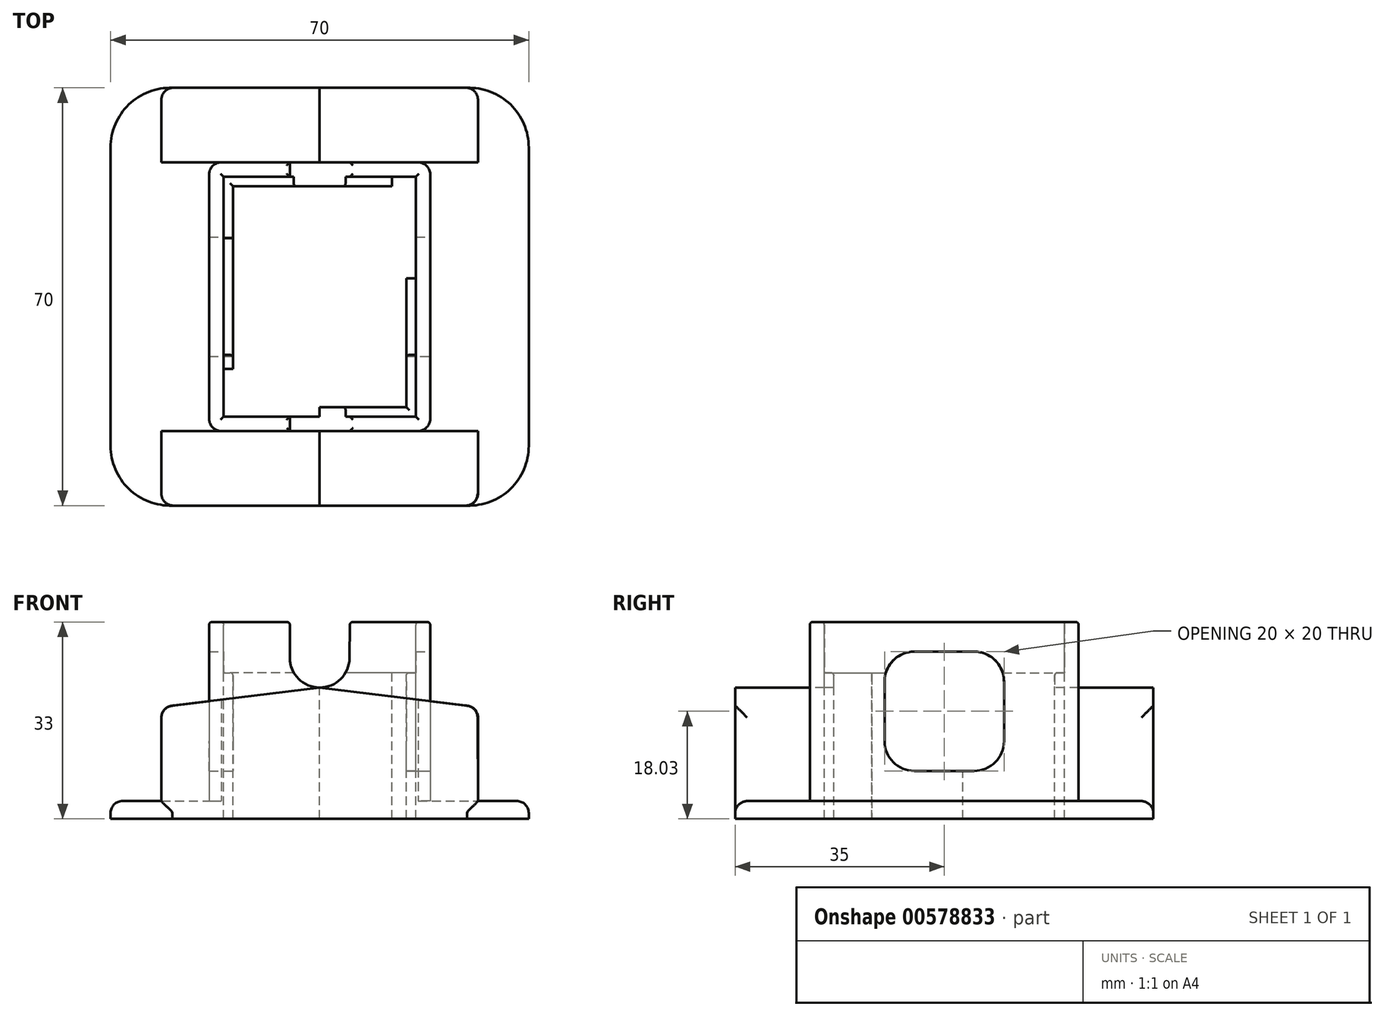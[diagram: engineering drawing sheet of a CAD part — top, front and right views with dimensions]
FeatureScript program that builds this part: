
annotation { "Feature Type Name" : "Feature", "Feature Type Description" : "" }
export const myFeature = defineFeature(function(context is Context, id is Id, definition is map)
    precondition{}
    {
        {
            var Q0;
            Q0=qCreatedBy(makeId("Top.planeOp"),FACE);
            var sketch = newSketch(context, id + "F0", { "sketchPlane" : qUnion([Q0])});
            skLineSegment(sketch, "E0.bottom", {"start": v(25, -35) * mm, "end": v(-25, -35) * mm});
            skLineSegment(sketch, "E0.top", {"start": v(25, 35) * mm, "end": v(-25, 35) * mm});
            skLineSegment(sketch, "E0.left", {"start": v(35, -25) * mm, "end": v(35, 25) * mm});
            skLineSegment(sketch, "E0.right", {"start": v(-35, -25) * mm, "end": v(-35, 25) * mm});
            skPoint(sketch, "E0.middle", {"position": v(0, 0) * mm});
            skPoint(sketch, "E1.visualSharp", {"position": v(-35, -35) * mm});
            skArc(sketch, "E1.filletArc", {"start": v(-35, -25) * mm, "mid": v(-32.07, -32.07) * mm, "end": v(-25, -35) * mm});
            skPoint(sketch, "E2.visualSharp", {"position": v(35, -35) * mm});
            skArc(sketch, "E2.filletArc", {"start": v(25, -35) * mm, "mid": v(32.07, -32.07) * mm, "end": v(35, -25) * mm});
            skPoint(sketch, "E3.visualSharp", {"position": v(35, 35) * mm});
            skArc(sketch, "E3.filletArc", {"start": v(35, 25) * mm, "mid": v(32.07, 32.07) * mm, "end": v(25, 35) * mm});
            skPoint(sketch, "E4.visualSharp", {"position": v(-35, 35) * mm});
            skArc(sketch, "E4.filletArc", {"start": v(-25, 35) * mm, "mid": v(-32.07, 32.07) * mm, "end": v(-35, 25) * mm});
            skSolve(sketch);
        }
        {
            var Q0;
            Q0=qSketchRegion(id+"F0",true);
            extrude(context, id + "F1", {"entities" : qUnion([Q0]), "depth" : 3 * mm, "offsetDistance" : 25 * mm});
        }
        {
            var Q0;
            Q0=makeQuery(id+"F1.opExtrude","CAP_FACE",FACE,{"disambiguationData":[OSD([sQuery(id+"F0.wireOp",EDGE,"E0.bottom"),sQuery(id+"F0.wireOp",EDGE,"E0.top"),sQuery(id+"F0.wireOp",EDGE,"E0.left"),sQuery(id+"F0.wireOp",EDGE,"E0.right"),sQuery(id+"F0.wireOp",EDGE,"E1.filletArc"),sQuery(id+"F0.wireOp",EDGE,"E2.filletArc"),sQuery(id+"F0.wireOp",EDGE,"E3.filletArc"),sQuery(id+"F0.wireOp",EDGE,"E4.filletArc")])],"isStart":false});
            var sketch = newSketch(context, id + "F2", { "sketchPlane" : qUnion([Q0])});
            skLineSegment(sketch, "E5.bottom", {"start": v(16.5, -22.5) * mm, "end": v(-16.5, -22.5) * mm});
            skLineSegment(sketch, "E5.top", {"start": v(16.5, 22.5) * mm, "end": v(-16.5, 22.5) * mm});
            skLineSegment(sketch, "E5.left", {"start": v(18.5, -20.5) * mm, "end": v(18.5, 20.5) * mm});
            skLineSegment(sketch, "E5.right", {"start": v(-18.5, -20.5) * mm, "end": v(-18.5, 20.5) * mm});
            skPoint(sketch, "E5.middle", {"position": v(0, 0) * mm});
            skPoint(sketch, "E6.visualSharp", {"position": v(18.5, -22.5) * mm});
            skArc(sketch, "E6.filletArc", {"start": v(16.5, -22.5) * mm, "mid": v(17.91, -21.91) * mm, "end": v(18.5, -20.5) * mm});
            skPoint(sketch, "E7.visualSharp", {"position": v(18.5, 22.5) * mm});
            skArc(sketch, "E7.filletArc", {"start": v(18.5, 20.5) * mm, "mid": v(17.91, 21.91) * mm, "end": v(16.5, 22.5) * mm});
            skPoint(sketch, "E8.visualSharp", {"position": v(-18.5, 22.5) * mm});
            skArc(sketch, "E8.filletArc", {"start": v(-16.5, 22.5) * mm, "mid": v(-17.91, 21.91) * mm, "end": v(-18.5, 20.5) * mm});
            skPoint(sketch, "E9.visualSharp", {"position": v(-18.5, -22.5) * mm});
            skArc(sketch, "E9.filletArc", {"start": v(-18.5, -20.5) * mm, "mid": v(-17.91, -21.91) * mm, "end": v(-16.5, -22.5) * mm});
            skSolve(sketch);
        }
        {
            var Q0;
            Q0=makeQuery(id+"F2.imprint","IMPRINT",FACE,{"disambiguationData":[TD([[makeQuery(id+"F2.imprint","IMPRINT",EDGE,{"derivedFrom":sQuery(id+"F2.wireOp",EDGE,"E5.bottom")}),-1.0]])]});
            extrude(context, id + "F3", {"entities" : qUnion([Q0]), "operationType" : NewBodyOperationType.ADD, "depth" : 30 * mm, "offsetDistance" : 25 * mm});
        }
        {
            var Q0;
            Q0=makeQuery(id+"F3.opExtrude","CAP_FACE",FACE,{"disambiguationData":[OSD([sQuery(id+"F2.wireOp",EDGE,"E5.bottom"),sQuery(id+"F2.wireOp",EDGE,"E5.top"),sQuery(id+"F2.wireOp",EDGE,"E5.left"),sQuery(id+"F2.wireOp",EDGE,"E5.right"),sQuery(id+"F2.wireOp",EDGE,"E6.filletArc"),sQuery(id+"F2.wireOp",EDGE,"E7.filletArc"),sQuery(id+"F2.wireOp",EDGE,"E8.filletArc"),sQuery(id+"F2.wireOp",EDGE,"E9.filletArc")])],"isStart":false});
            var sketch = newSketch(context, id + "F4", { "sketchPlane" : qUnion([Q0])});
            skLineSegment(sketch, "E10.bottom", {"start": v(-14.5, 18.5) * mm, "end": v(14.5, 18.5) * mm});
            skLineSegment(sketch, "E10.top", {"start": v(-14.5, -18.5) * mm, "end": v(14.5, -18.5) * mm});
            skLineSegment(sketch, "E10.left", {"start": v(-14.5, 18.5) * mm, "end": v(-14.5, -18.5) * mm});
            skLineSegment(sketch, "E10.right", {"start": v(14.5, 18.5) * mm, "end": v(14.5, -18.5) * mm});
            skPoint(sketch, "E10.middle", {"position": v(0, 0) * mm});
            skSolve(sketch);
        }
        {
            var Q0;
            Q0=makeQuery(id+"F4.imprint","IMPRINT",FACE,{"disambiguationData":[TD([[makeQuery(id+"F4.imprint","IMPRINT",EDGE,{"derivedFrom":sQuery(id+"F4.wireOp",EDGE,"E10.bottom")}),-1.0]])]});
            extrude(context, id + "F5", {"entities" : qUnion([Q0]), "operationType" : NewBodyOperationType.REMOVE, "endBound" : BoundingType.THROUGH_ALL, "oppositeDirection" : true, "depth" : 25 * mm});
        }
        {
            var Q0;
            Q0=makeQuery(id+"F3.opExtrude","CAP_FACE",FACE,{"disambiguationData":[OSD([sQuery(id+"F2.wireOp",EDGE,"E5.bottom"),sQuery(id+"F2.wireOp",EDGE,"E5.top"),sQuery(id+"F2.wireOp",EDGE,"E5.left"),sQuery(id+"F2.wireOp",EDGE,"E5.right"),sQuery(id+"F2.wireOp",EDGE,"E6.filletArc"),sQuery(id+"F2.wireOp",EDGE,"E7.filletArc"),sQuery(id+"F2.wireOp",EDGE,"E8.filletArc"),sQuery(id+"F2.wireOp",EDGE,"E9.filletArc")])],"isStart":false});
            var sketch = newSketch(context, id + "F6", { "sketchPlane" : qUnion([Q0])});
            skLineSegment(sketch, "E11.bottom", {"start": v(16.1, -20.1) * mm, "end": v(-16.1, -20.1) * mm});
            skLineSegment(sketch, "E11.top", {"start": v(16.1, 20.1) * mm, "end": v(-16.1, 20.1) * mm});
            skLineSegment(sketch, "E11.left", {"start": v(16.1, -20.1) * mm, "end": v(16.1, 20.1) * mm});
            skLineSegment(sketch, "E11.right", {"start": v(-16.1, -20.1) * mm, "end": v(-16.1, 20.1) * mm});
            skPoint(sketch, "E11.middle", {"position": v(0, 0) * mm});
            skSolve(sketch);
        }
        {
            var Q0;
            Q0=qSketchRegion(id+"F6",true);
            extrude(context, id + "F7", {"entities" : qUnion([Q0]), "operationType" : NewBodyOperationType.REMOVE, "oppositeDirection" : true, "depth" : 8.5 * mm, "offsetDistance" : 25 * mm});
        }
        {
            var Q0;
            Q0=makeQuery(id+"F7.boolean.opBoolean","COPY",FACE,{"derivedFrom":makeQuery(id+"F7.opExtrude","CAP_FACE",FACE,{"disambiguationData":[OSD([sQuery(id+"F6.wireOp",EDGE,"E11.bottom"),sQuery(id+"F6.wireOp",EDGE,"E11.top"),sQuery(id+"F6.wireOp",EDGE,"E11.left"),sQuery(id+"F6.wireOp",EDGE,"E11.right")])],"isStart":false})});
            var sketch = newSketch(context, id + "F8", { "sketchPlane" : qUnion([Q0])});
            skLineSegment(sketch, "E12.bottom", {"start": v(12.1, 20.1) * mm, "end": v(16.1, 20.1) * mm});
            skLineSegment(sketch, "E12.top", {"start": v(12.1, 3.1) * mm, "end": v(16.1, 3.1) * mm});
            skLineSegment(sketch, "E12.left", {"start": v(12.1, 20.1) * mm, "end": v(12.1, 3.1) * mm});
            skLineSegment(sketch, "E12.right", {"start": v(16.1, 20.1) * mm, "end": v(16.1, 3.1) * mm});
            skSolve(sketch);
        }
        {
            var Q0;
            {var subQ0=sQuery(id+"F8.wireOp",EDGE,"E12.right");var subQ1=sQuery(id+"F8.wireOp",EDGE,"E12.top");var subQ2=makeQuery(id+"F8.imprint","INTERSECT",VERTEX,{"derivedFrom":[subQ1,subQ0]});Q0=makeQuery(id+"F8.imprint","IMPRINT",FACE,{"disambiguationData":[TD([[makeQuery(id+"F8.imprint","IMPRINT",EDGE,{"disambiguationData":[TD([[subQ2,1.0]])],"derivedFrom":subQ1}),1.0]])]});}
            var Q1;
            {var subQ1=sQuery(id+"F8.wireOp",EDGE,"E12.bottom");Q1=makeQuery(id+"F8.imprint","IMPRINT",FACE,{"disambiguationData":[TD([[makeQuery(id+"F8.imprint","IMPRINT",EDGE,{"derivedFrom":subQ1}),1.0]])]});}
            extrude(context, id + "F9", {"entities" : qUnion([Q0, Q1]), "operationType" : NewBodyOperationType.REMOVE, "endBound" : BoundingType.THROUGH_ALL, "oppositeDirection" : true, "depth" : 22 * mm, "offsetDistance" : 25 * mm});
        }
        {
            var Q0;
            Q0=makeQuery(id+"F3.opExtrude","CAP_FACE",FACE,{"disambiguationData":[OSD([sQuery(id+"F2.wireOp",EDGE,"E5.bottom"),sQuery(id+"F2.wireOp",EDGE,"E5.top"),sQuery(id+"F2.wireOp",EDGE,"E5.left"),sQuery(id+"F2.wireOp",EDGE,"E5.right"),sQuery(id+"F2.wireOp",EDGE,"E6.filletArc"),sQuery(id+"F2.wireOp",EDGE,"E7.filletArc"),sQuery(id+"F2.wireOp",EDGE,"E8.filletArc"),sQuery(id+"F2.wireOp",EDGE,"E9.filletArc")])],"isStart":false});
            var sketch = newSketch(context, id + "F10", { "sketchPlane" : qUnion([Q0])});
            skLineSegment(sketch, "E13.bottom", {"start": v(0, -20.1) * mm, "end": v(-16.1, -20.1) * mm});
            skLineSegment(sketch, "E13.top", {"start": v(0, -12.1) * mm, "end": v(-16.1, -12.1) * mm});
            skLineSegment(sketch, "E13.left", {"start": v(0, -20.1) * mm, "end": v(0, -12.1) * mm});
            skLineSegment(sketch, "E13.right", {"start": v(-16.1, -20.1) * mm, "end": v(-16.1, -12.1) * mm});
            skSolve(sketch);
        }
        {
            var Q0;
            Q0=qSketchRegion(id+"F10",true);
            extrude(context, id + "F11", {"entities" : qUnion([Q0]), "operationType" : NewBodyOperationType.REMOVE, "endBound" : BoundingType.THROUGH_ALL, "oppositeDirection" : true, "depth" : 20 * mm, "offsetDistance" : 25 * mm});
        }
        {
            var Q0;
            Q0=makeQuery(id+"F3.opExtrude","SWEPT_FACE",FACE,{"disambiguationData":[OSD([sQuery(id+"F2.wireOp",EDGE,"E5.left")])]});
            var sketch = newSketch(context, id + "F12", { "sketchPlane" : qUnion([Q0])});
            skLineSegment(sketch, "E14.bottom", {"start": v(5, 8.03) * mm, "end": v(-5, 8.03) * mm});
            skLineSegment(sketch, "E14.top", {"start": v(5, 28.03) * mm, "end": v(-5, 28.03) * mm});
            skLineSegment(sketch, "E14.left", {"start": v(10, 13.03) * mm, "end": v(10, 23.03) * mm});
            skLineSegment(sketch, "E14.right", {"start": v(-10, 13.03) * mm, "end": v(-10, 23.03) * mm});
            skPoint(sketch, "E14.middle", {"position": v(0, 18.03) * mm});
            skPoint(sketch, "E15.visualSharp", {"position": v(10, 8.03) * mm});
            skArc(sketch, "E15.filletArc", {"start": v(5, 8.03) * mm, "mid": v(8.54, 9.5) * mm, "end": v(10, 13.03) * mm});
            skPoint(sketch, "E16.visualSharp", {"position": v(-10, 8.03) * mm});
            skArc(sketch, "E16.filletArc", {"start": v(-10, 13.03) * mm, "mid": v(-8.54, 9.5) * mm, "end": v(-5, 8.03) * mm});
            skPoint(sketch, "E17.visualSharp", {"position": v(-10, 28.03) * mm});
            skArc(sketch, "E17.filletArc", {"start": v(-5, 28.03) * mm, "mid": v(-8.54, 26.57) * mm, "end": v(-10, 23.03) * mm});
            skPoint(sketch, "E18.visualSharp", {"position": v(10, 28.03) * mm});
            skArc(sketch, "E18.filletArc", {"start": v(10, 23.03) * mm, "mid": v(8.54, 26.57) * mm, "end": v(5, 28.03) * mm});
            skSolve(sketch);
        }
        {
            var Q0;
            Q0=qSketchRegion(id+"F12",true);
            extrude(context, id + "F13", {"entities" : qUnion([Q0]), "operationType" : NewBodyOperationType.REMOVE, "endBound" : BoundingType.THROUGH_ALL, "oppositeDirection" : true, "depth" : 25 * mm, "offsetDistance" : 25 * mm, "hasSecondDirection" : true, "secondDirectionBound" : SecondDirectionBoundingType.THROUGH_ALL, "secondDirectionOppositeDirection" : false, "secondDirectionDepth" : 25 * mm});
        }
        {
            var Q0;
            Q0=makeQuery(id+"F3.opExtrude","SWEPT_FACE",FACE,{"disambiguationData":[OSD([sQuery(id+"F2.wireOp",EDGE,"E5.bottom")])]});
            var sketch = newSketch(context, id + "F14", { "sketchPlane" : qUnion([Q0])});
            skArc(sketch, "E19", {"start": v(-5, 27) * mm, "mid": v(-0.03, 22) * mm, "end": v(5, 26.94) * mm});
            skLineSegment(sketch, "E20", {"start": v(-5, 27) * mm, "end": v(-5, 33) * mm});
            skLineSegment(sketch, "E21", {"start": v(-5, 33) * mm, "end": v(5.07, 33) * mm});
            skLineSegment(sketch, "E22", {"start": v(5.07, 33) * mm, "end": v(5, 26.94) * mm});
            skSolve(sketch);
        }
        {
            var Q0;
            Q0=qSketchRegion(id+"F14",true);
            extrude(context, id + "F15", {"entities" : qUnion([Q0]), "operationType" : NewBodyOperationType.REMOVE, "endBound" : BoundingType.THROUGH_ALL, "oppositeDirection" : true, "depth" : 25 * mm, "offsetDistance" : 25 * mm});
        }
        {
            var Q0;
            Q0=makeQuery(id+"F3.opExtrude","SWEPT_FACE",FACE,{"disambiguationData":[OSD([sQuery(id+"F2.wireOp",EDGE,"E5.bottom")])]});
            var sketch = newSketch(context, id + "F16", { "sketchPlane" : qUnion([Q0])});
            skLineSegment(sketch, "E23.top", {"start": v(-16.5, 3) * mm, "end": v(16.5, 3) * mm});
            skLineSegment(sketch, "E24", {"start": v(0, 22) * mm, "end": v(16.5, 19.97) * mm});
            skLineSegment(sketch, "E25", {"start": v(0, 22) * mm, "end": v(-16.5, 19.97) * mm});
            skLineSegment(sketch, "E26", {"start": v(16.5, 19.97) * mm, "end": v(26.43, 18.76) * mm});
            skLineSegment(sketch, "E27", {"start": v(-16.5, 19.97) * mm, "end": v(-26.5, 18.75) * mm});
            skLineSegment(sketch, "E28", {"start": v(-16.5, 3) * mm, "end": v(-26.5, 3) * mm});
            skLineSegment(sketch, "E29", {"start": v(-26.5, 3) * mm, "end": v(-26.5, 18.75) * mm});
            skLineSegment(sketch, "E30", {"start": v(16.5, 3) * mm, "end": v(26.5, 3) * mm});
            skLineSegment(sketch, "E31", {"start": v(26.5, 3) * mm, "end": v(26.43, 18.76) * mm});
            skPoint(sketch, "E32.orphan", {"position": v(36.35, 17.54) * mm});
            skSolve(sketch);
        }
        {
            var Q0;
            Q0=qSketchRegion(id+"F16",true);
            var Q1;
            Q1=makeQuery(id+"F1.opExtrude","SWEPT_FACE",FACE,{"disambiguationData":[OSD([sQuery(id+"F0.wireOp",EDGE,"E0.bottom")])]});
            extrude(context, id + "F17", {"entities" : qUnion([Q0]), "operationType" : NewBodyOperationType.ADD, "endBound" : BoundingType.UP_TO_SURFACE, "depth" : 25 * mm, "endBoundEntityFace" : qUnion([Q1]), "offsetDistance" : 25 * mm});
        }
        {
            var Q0;
            Q0=makeQuery(id+"F3.opExtrude","SWEPT_FACE",FACE,{"disambiguationData":[OSD([sQuery(id+"F2.wireOp",EDGE,"E5.top")])]});
            var sketch = newSketch(context, id + "F18", { "sketchPlane" : qUnion([Q0])});
            skLineSegment(sketch, "E33.top", {"start": v(-16.5, 3) * mm, "end": v(16.5, 3) * mm});
            skLineSegment(sketch, "E34", {"start": v(0, 22) * mm, "end": v(-16.5, 19.97) * mm});
            skLineSegment(sketch, "E35", {"start": v(0, 22) * mm, "end": v(16.5, 19.97) * mm});
            skLineSegment(sketch, "E36", {"start": v(-16.5, 19.97) * mm, "end": v(-26.5, 18.75) * mm});
            skLineSegment(sketch, "E37", {"start": v(16.5, 19.97) * mm, "end": v(26.5, 18.75) * mm});
            skLineSegment(sketch, "E38", {"start": v(-16.5, 3) * mm, "end": v(-26.5, 3) * mm});
            skLineSegment(sketch, "E39", {"start": v(-26.5, 3) * mm, "end": v(-26.5, 18.75) * mm});
            skLineSegment(sketch, "E40", {"start": v(16.5, 3) * mm, "end": v(26.5, 3) * mm});
            skLineSegment(sketch, "E41", {"start": v(26.5, 3) * mm, "end": v(26.5, 18.75) * mm});
            skSolve(sketch);
        }
        {
            var Q0;
            Q0=qSketchRegion(id+"F18",true);
            var Q1;
            Q1=makeQuery(id+"F1.opExtrude","SWEPT_FACE",FACE,{"disambiguationData":[OSD([sQuery(id+"F0.wireOp",EDGE,"E0.top")])]});
            extrude(context, id + "F19", {"entities" : qUnion([Q0]), "operationType" : NewBodyOperationType.ADD, "endBound" : BoundingType.UP_TO_SURFACE, "depth" : 25 * mm, "endBoundEntityFace" : qUnion([Q1]), "offsetDistance" : 25 * mm});
        }
        {
            var Q0;
            {var subQ0=sQuery(id+"F0.wireOp",EDGE,"E3.filletArc");Q0=makeQuery(id+"F19.boolean.opBoolean","SPLIT",EDGE,{"disambiguationData":[topologyDisambiguationEdgeConnected([makeQuery(id+"F1.opExtrude","CAP_FACE",FACE,{"disambiguationData":[OSD([sQuery(id+"F0.wireOp",EDGE,"E0.bottom"),sQuery(id+"F0.wireOp",EDGE,"E0.top"),sQuery(id+"F0.wireOp",EDGE,"E0.left"),sQuery(id+"F0.wireOp",EDGE,"E0.right"),sQuery(id+"F0.wireOp",EDGE,"E1.filletArc"),sQuery(id+"F0.wireOp",EDGE,"E2.filletArc"),subQ0,sQuery(id+"F0.wireOp",EDGE,"E4.filletArc")])],"isStart":false})])],"derivedFrom":makeQuery(id+"F1.opExtrude","CAP_EDGE",EDGE,{"disambiguationData":[OSD([subQ0])],"isStart":false})});}
            var Q1;
            Q1=makeQuery(id+"F19.opExtrude","SWEPT_EDGE",EDGE,{"disambiguationData":[OSD([sQuery(id+"F18.wireOp",EDGE,"E36"),sQuery(id+"F18.wireOp",EDGE,"E39")])]});
            var Q2;
            Q2=makeQuery(id+"F17.opExtrude","SWEPT_EDGE",EDGE,{"disambiguationData":[OSD([sQuery(id+"F16.wireOp",EDGE,"E26"),sQuery(id+"F16.wireOp",EDGE,"E31")])]});
            var Q3;
            Q3=makeQuery(id+"F17.opExtrude","CAP_EDGE",EDGE,{"disambiguationData":[OSD([sQuery(id+"F16.wireOp",EDGE,"E31")])],"isStart":false});
            var Q4;
            Q4=makeQuery(id+"F19.opExtrude","CAP_EDGE",EDGE,{"disambiguationData":[OSD([sQuery(id+"F18.wireOp",EDGE,"E39")])],"isStart":false});
            var Q5;
            Q5=makeQuery(id+"F17.opExtrude","CAP_EDGE",EDGE,{"disambiguationData":[OSD([sQuery(id+"F16.wireOp",EDGE,"E29")])],"isStart":false});
            var Q6;
            Q6=makeQuery(id+"F19.opExtrude","CAP_EDGE",EDGE,{"disambiguationData":[OSD([sQuery(id+"F18.wireOp",EDGE,"E41")])],"isStart":false});
            var Q7;
            Q7=makeQuery(id+"F17.opExtrude","SWEPT_EDGE",EDGE,{"disambiguationData":[OSD([sQuery(id+"F16.wireOp",EDGE,"E27"),sQuery(id+"F16.wireOp",EDGE,"E29")])]});
            var Q8;
            Q8=makeQuery(id+"F19.opExtrude","SWEPT_EDGE",EDGE,{"disambiguationData":[OSD([sQuery(id+"F18.wireOp",EDGE,"E37"),sQuery(id+"F18.wireOp",EDGE,"E41")])]});
            var Q9;
            Q9=makeQuery(id+"F1.opExtrude","CAP_EDGE",EDGE,{"disambiguationData":[OSD([sQuery(id+"F0.wireOp",EDGE,"E0.right")])],"isStart":false});
            fillet(context, id + "F20", {"entities" : qUnion([Q0, Q1, Q2, Q3, Q4, Q5, Q6, Q7, Q8, Q9]), "radius" : 2 * mm, "tangentPropagation" : true, "allowEdgeOverflow" : false});
        }
        {
            var Q0;
            {var subQ0=sQuery(id+"F2.wireOp",EDGE,"E7.filletArc");var subQ1=sQuery(id+"F2.wireOp",EDGE,"E5.bottom");var subQ2=sQuery(id+"F2.wireOp",EDGE,"E5.top");var subQ3=sQuery(id+"F2.wireOp",EDGE,"E5.left");var subQ4=sQuery(id+"F2.wireOp",EDGE,"E6.filletArc");Q0=makeQuery(id+"F15.boolean.opBoolean","SPLIT",FACE,{"disambiguationData":[TD([makeQuery(id+"F3.opExtrude","SWEPT_FACE",FACE,{"disambiguationData":[OSD([subQ3])]})])],"derivedFrom":makeQuery(id+"F3.opExtrude","CAP_FACE",FACE,{"disambiguationData":[OSD([subQ1,subQ2,subQ3,sQuery(id+"F2.wireOp",EDGE,"E5.right"),subQ4,subQ0,sQuery(id+"F2.wireOp",EDGE,"E8.filletArc"),sQuery(id+"F2.wireOp",EDGE,"E9.filletArc")])],"isStart":false})});}
            var Q1;
            {var subQ0=sQuery(id+"F2.wireOp",EDGE,"E9.filletArc");var subQ1=sQuery(id+"F2.wireOp",EDGE,"E5.bottom");var subQ2=sQuery(id+"F2.wireOp",EDGE,"E5.right");var subQ3=sQuery(id+"F2.wireOp",EDGE,"E5.top");var subQ4=sQuery(id+"F2.wireOp",EDGE,"E8.filletArc");Q1=makeQuery(id+"F15.boolean.opBoolean","SPLIT",FACE,{"disambiguationData":[TD([makeQuery(id+"F3.opExtrude","SWEPT_FACE",FACE,{"disambiguationData":[OSD([subQ2])]})])],"derivedFrom":makeQuery(id+"F3.opExtrude","CAP_FACE",FACE,{"disambiguationData":[OSD([subQ1,subQ3,sQuery(id+"F2.wireOp",EDGE,"E5.left"),subQ2,sQuery(id+"F2.wireOp",EDGE,"E6.filletArc"),sQuery(id+"F2.wireOp",EDGE,"E7.filletArc"),subQ4,subQ0])],"isStart":false})});}
            var Q2;
            Q2=makeQuery(id+"F7.boolean.opBoolean","INTERSECT",EDGE,{"derivedFrom":[makeQuery(id+"F5.boolean.opBoolean","COPY",FACE,{"derivedFrom":makeQuery(id+"F5.opExtrude","SWEPT_FACE",FACE,{"disambiguationData":[OSD([sQuery(id+"F4.wireOp",EDGE,"E10.right")])]})}),makeQuery(id+"F7.opExtrude","CAP_FACE",FACE,{"disambiguationData":[OSD([sQuery(id+"F6.wireOp",EDGE,"E11.bottom"),sQuery(id+"F6.wireOp",EDGE,"E11.top"),sQuery(id+"F6.wireOp",EDGE,"E11.left"),sQuery(id+"F6.wireOp",EDGE,"E11.right")])],"isStart":false})]});
            var Q3;
            Q3=makeQuery(id+"F7.boolean.opBoolean","INTERSECT",EDGE,{"derivedFrom":[makeQuery(id+"F5.boolean.opBoolean","COPY",FACE,{"derivedFrom":makeQuery(id+"F5.opExtrude","SWEPT_FACE",FACE,{"disambiguationData":[OSD([sQuery(id+"F4.wireOp",EDGE,"E10.top")])]})}),makeQuery(id+"F7.opExtrude","CAP_FACE",FACE,{"disambiguationData":[OSD([sQuery(id+"F6.wireOp",EDGE,"E11.bottom"),sQuery(id+"F6.wireOp",EDGE,"E11.top"),sQuery(id+"F6.wireOp",EDGE,"E11.left"),sQuery(id+"F6.wireOp",EDGE,"E11.right")])],"isStart":false})]});
            var Q4;
            {var subQ0=makeQuery(id+"F5.boolean.opBoolean","COPY",FACE,{"derivedFrom":makeQuery(id+"F5.opExtrude","SWEPT_FACE",FACE,{"disambiguationData":[OSD([sQuery(id+"F4.wireOp",EDGE,"E10.left")])]})});var subQ1=makeQuery(id+"F7.opExtrude","CAP_FACE",FACE,{"disambiguationData":[OSD([sQuery(id+"F6.wireOp",EDGE,"E11.bottom"),sQuery(id+"F6.wireOp",EDGE,"E11.top"),sQuery(id+"F6.wireOp",EDGE,"E11.left"),sQuery(id+"F6.wireOp",EDGE,"E11.right")])],"isStart":false});Q4=makeQuery(id+"F13.boolean.opBoolean","SPLIT",EDGE,{"disambiguationData":[TD([makeQuery(id+"F11.boolean.opBoolean","COPY",FACE,{"derivedFrom":makeQuery(id+"F11.opExtrude","SWEPT_FACE",FACE,{"disambiguationData":[OSD([sQuery(id+"F10.wireOp",EDGE,"E13.top")])]})})])],"derivedFrom":makeQuery(id+"F7.boolean.opBoolean","INTERSECT",EDGE,{"derivedFrom":[subQ0,subQ1]})});}
            var Q5;
            {var subQ0=makeQuery(id+"F7.opExtrude","CAP_FACE",FACE,{"disambiguationData":[OSD([sQuery(id+"F6.wireOp",EDGE,"E11.bottom"),sQuery(id+"F6.wireOp",EDGE,"E11.top"),sQuery(id+"F6.wireOp",EDGE,"E11.left"),sQuery(id+"F6.wireOp",EDGE,"E11.right")])],"isStart":false});var subQ1=makeQuery(id+"F5.boolean.opBoolean","COPY",FACE,{"derivedFrom":makeQuery(id+"F5.opExtrude","SWEPT_FACE",FACE,{"disambiguationData":[OSD([sQuery(id+"F4.wireOp",EDGE,"E10.left")])]})});Q5=makeQuery(id+"F13.boolean.opBoolean","SPLIT",EDGE,{"disambiguationData":[TD([makeQuery(id+"F5.boolean.opBoolean","COPY",FACE,{"derivedFrom":makeQuery(id+"F5.opExtrude","SWEPT_FACE",FACE,{"disambiguationData":[OSD([sQuery(id+"F4.wireOp",EDGE,"E10.bottom")])]})})])],"derivedFrom":makeQuery(id+"F7.boolean.opBoolean","INTERSECT",EDGE,{"derivedFrom":[subQ1,subQ0]})});}
            var Q6;
            {var subQ0=makeQuery(id+"F5.boolean.opBoolean","COPY",FACE,{"derivedFrom":makeQuery(id+"F5.opExtrude","SWEPT_FACE",FACE,{"disambiguationData":[OSD([sQuery(id+"F4.wireOp",EDGE,"E10.bottom")])]})});var subQ1=makeQuery(id+"F7.opExtrude","CAP_FACE",FACE,{"disambiguationData":[OSD([sQuery(id+"F6.wireOp",EDGE,"E11.bottom"),sQuery(id+"F6.wireOp",EDGE,"E11.top"),sQuery(id+"F6.wireOp",EDGE,"E11.left"),sQuery(id+"F6.wireOp",EDGE,"E11.right")])],"isStart":false});Q6=makeQuery(id+"F15.boolean.opBoolean","SPLIT",EDGE,{"disambiguationData":[TD([makeQuery(id+"F5.boolean.opBoolean","COPY",FACE,{"derivedFrom":makeQuery(id+"F5.opExtrude","SWEPT_FACE",FACE,{"disambiguationData":[OSD([sQuery(id+"F4.wireOp",EDGE,"E10.left")])]})})])],"derivedFrom":makeQuery(id+"F7.boolean.opBoolean","INTERSECT",EDGE,{"derivedFrom":[subQ0,subQ1]})});}
            var Q7;
            {var subQ0=makeQuery(id+"F5.boolean.opBoolean","COPY",FACE,{"derivedFrom":makeQuery(id+"F5.opExtrude","SWEPT_FACE",FACE,{"disambiguationData":[OSD([sQuery(id+"F4.wireOp",EDGE,"E10.bottom")])]})});var subQ1=makeQuery(id+"F7.opExtrude","CAP_FACE",FACE,{"disambiguationData":[OSD([sQuery(id+"F6.wireOp",EDGE,"E11.bottom"),sQuery(id+"F6.wireOp",EDGE,"E11.top"),sQuery(id+"F6.wireOp",EDGE,"E11.left"),sQuery(id+"F6.wireOp",EDGE,"E11.right")])],"isStart":false});Q7=makeQuery(id+"F15.boolean.opBoolean","SPLIT",EDGE,{"disambiguationData":[TD([makeQuery(id+"F9.boolean.opBoolean","COPY",FACE,{"derivedFrom":makeQuery(id+"F9.opExtrude","SWEPT_FACE",FACE,{"disambiguationData":[OSD([sQuery(id+"F8.wireOp",EDGE,"E12.left")])]})})])],"derivedFrom":makeQuery(id+"F7.boolean.opBoolean","INTERSECT",EDGE,{"derivedFrom":[subQ0,subQ1]})});}
            fillet(context, id + "F21", {"entities" : qUnion([Q0, Q1, Q2, Q3, Q4, Q5, Q6, Q7]), "radius" : 0.5 * mm, "tangentPropagation" : true, "allowEdgeOverflow" : false});
        }
    });
